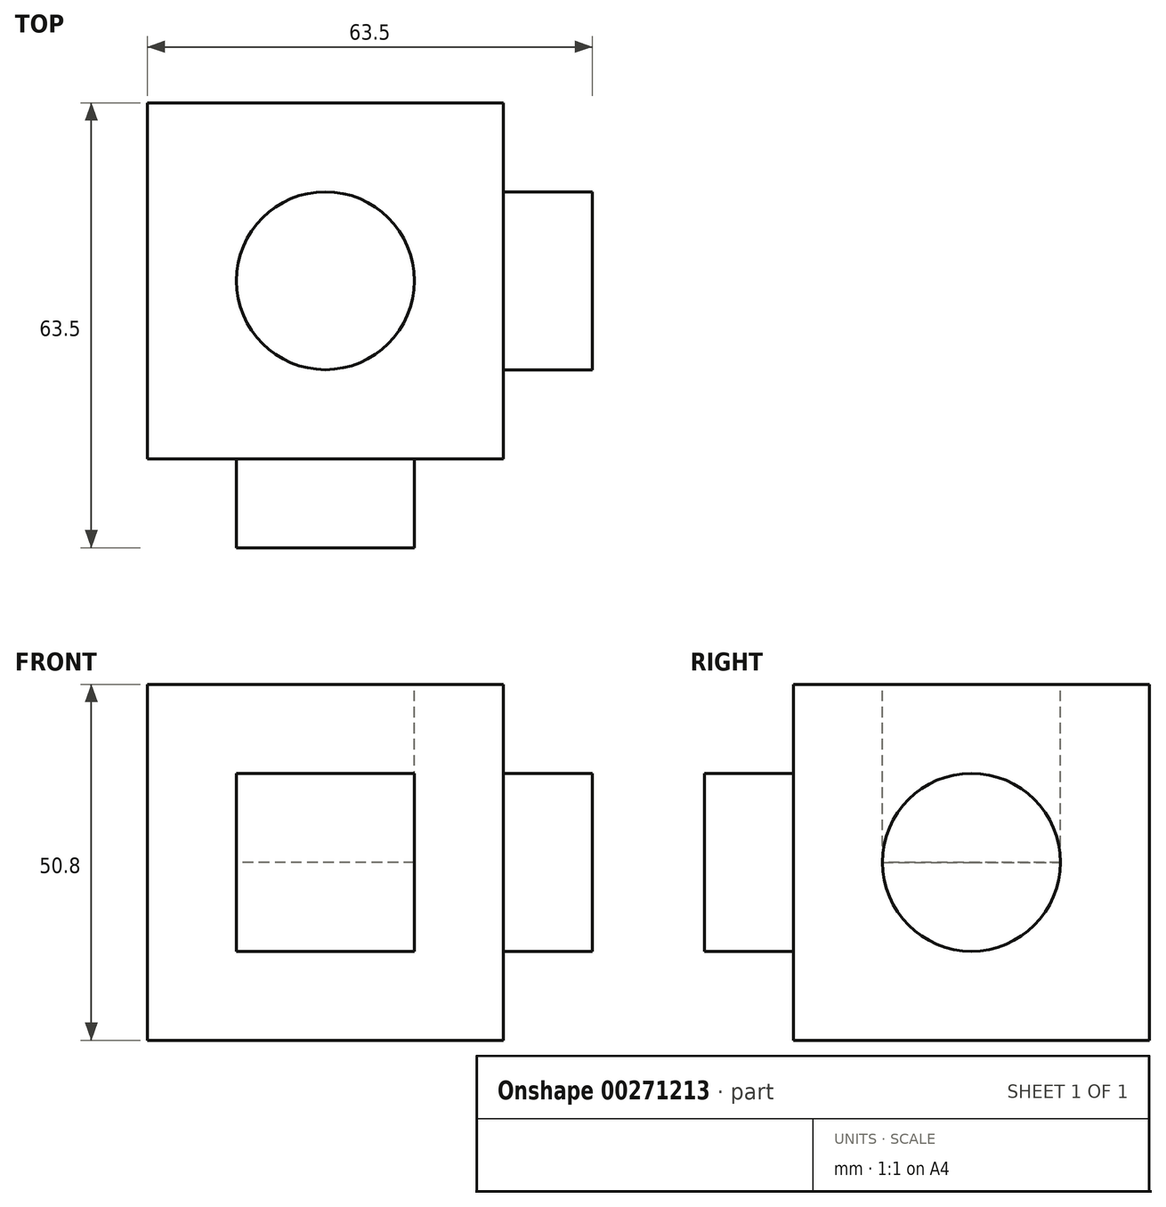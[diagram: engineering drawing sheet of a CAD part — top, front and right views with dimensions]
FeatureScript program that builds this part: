
annotation { "Feature Type Name" : "Feature", "Feature Type Description" : "" }
export const myFeature = defineFeature(function(context is Context, id is Id, definition is map)
    precondition{}
    {
        {
            var Q0;
            Q0=qCreatedBy(makeId("Front.planeOp"),FACE);
            var sketch = newSketch(context, id + "F0", { "sketchPlane" : qUnion([Q0])});
            skLineSegment(sketch, "E0.bottom", {"start": v(0, 0) * mm, "end": v(-50.8, 0) * mm});
            skLineSegment(sketch, "E0.top", {"start": v(0, 50.8) * mm, "end": v(-50.8, 50.8) * mm});
            skLineSegment(sketch, "E0.left", {"start": v(0, 0) * mm, "end": v(0, 50.8) * mm});
            skLineSegment(sketch, "E0.right", {"start": v(-50.8, 0) * mm, "end": v(-50.8, 50.8) * mm});
            skSolve(sketch);
        }
        {
            var Q0;
            Q0 = qSketchRegion(id + "F0", true);
            extrude(context, id + "F1", {"entities" : qUnion([Q0]), "depth" : 50.8 * mm});
        }
        {
            var Q0;
            Q0=makeQuery(id+"F1.opExtrude","CAP_FACE",FACE,{"disambiguationData":[OSD([sQuery(id+"F0.wireOp",EDGE,"E0.bottom"),sQuery(id+"F0.wireOp",EDGE,"E0.top"),sQuery(id+"F0.wireOp",EDGE,"E0.left"),sQuery(id+"F0.wireOp",EDGE,"E0.right")])],"isStart":false});
            var sketch = newSketch(context, id + "F2", { "sketchPlane" : qUnion([Q0])});
            skLineSegment(sketch, "E1.bottom", {"start": v(-38.1, 38.1) * mm, "end": v(-12.7, 38.1) * mm});
            skLineSegment(sketch, "E1.top", {"start": v(-38.1, 12.7) * mm, "end": v(-12.7, 12.7) * mm});
            skLineSegment(sketch, "E1.left", {"start": v(-38.1, 38.1) * mm, "end": v(-38.1, 12.7) * mm});
            skLineSegment(sketch, "E1.right", {"start": v(-12.7, 38.1) * mm, "end": v(-12.7, 12.7) * mm});
            skSolve(sketch);
        }
        {
            var Q0;
            Q0 = qSketchRegion(id + "F2", true);
            extrude(context, id + "F3", {"entities" : qUnion([Q0]), "operationType" : NewBodyOperationType.ADD, "depth" : 12.7 * mm});
        }
        {
            var Q0;
            Q0=makeQuery(id+"F1.opExtrude","SWEPT_FACE",FACE,{"disambiguationData":[OSD([sQuery(id+"F0.wireOp",EDGE,"E0.top")])]});
            var sketch = newSketch(context, id + "F4", { "sketchPlane" : qUnion([Q0])});
            skCircle(sketch, "E2", {"center": v(-25.4, -25.4) * mm, "radius": 12.7 * mm});
            skSolve(sketch);
        }
        {
            var Q0;
            Q0 = qSketchRegion(id + "F4", true);
            extrude(context, id + "F5", {"entities" : qUnion([Q0]), "operationType" : NewBodyOperationType.REMOVE, "oppositeDirection" : true, "depth" : 25.4 * mm});
        }
        {
            var Q0;
            Q0=makeQuery(id+"F1.opExtrude","SWEPT_FACE",FACE,{"disambiguationData":[OSD([sQuery(id+"F0.wireOp",EDGE,"E0.left")])]});
            var sketch = newSketch(context, id + "F6", { "sketchPlane" : qUnion([Q0])});
            skCircle(sketch, "E3", {"center": v(-25.4, 25.4) * mm, "radius": 12.7 * mm});
            skSolve(sketch);
        }
        {
            var Q0;
            Q0 = qSketchRegion(id + "F6", true);
            extrude(context, id + "F7", {"entities" : qUnion([Q0]), "operationType" : NewBodyOperationType.ADD, "depth" : 12.7 * mm});
        }
    });
